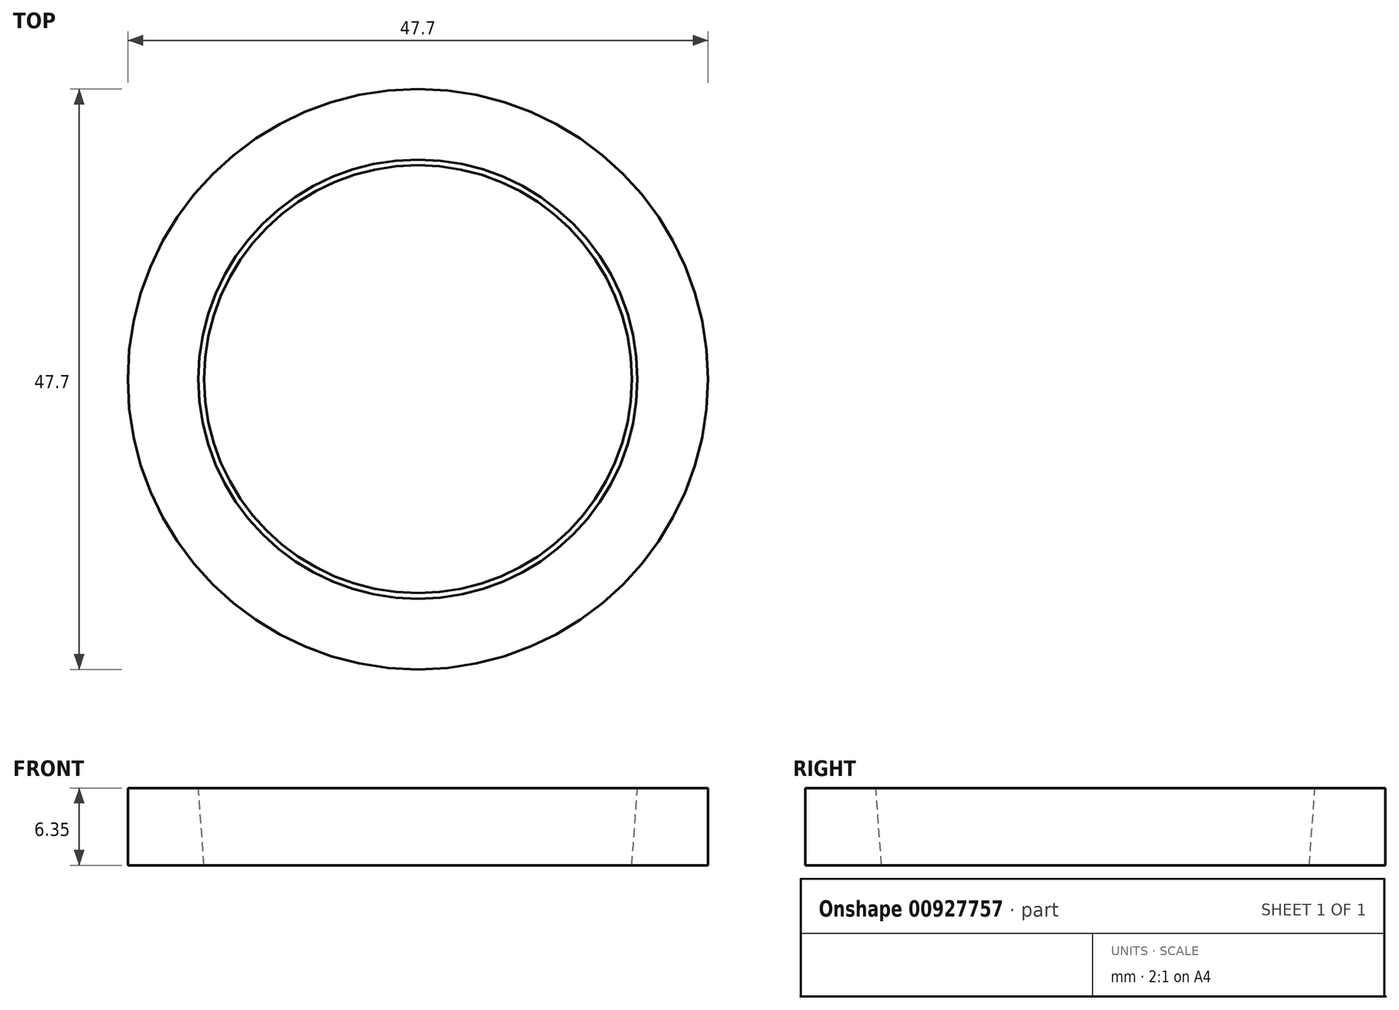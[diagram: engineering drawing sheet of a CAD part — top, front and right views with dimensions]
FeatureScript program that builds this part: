
annotation { "Feature Type Name" : "Feature", "Feature Type Description" : "" }
export const myFeature = defineFeature(function(context is Context, id is Id, definition is map)
    precondition{}
    {
        {
            var Q0;
            Q0=qCreatedBy(makeId("Top.planeOp"),FACE);
            var sketch = newSketch(context, id + "F0", { "sketchPlane" : qUnion([Q0])});
            skCircle(sketch, "E0", {"center": v(0, 0) * mm, "radius": 23.85 * mm});
            skCircle(sketch, "E1", {"center": v(0, 0) * mm, "radius": 15.88 * mm});
            skSolve(sketch);
        }
        {
            var Q0;
            Q0 = qSketchRegion(id + "F0", true);
            extrude(context, id + "F1", {"entities" : qUnion([Q0]), "depth" : 6.35 * mm, "offsetDistance" : 25.4 * mm});
        }
        {
            var Q0;
            Q0=qCreatedBy(makeId("Front.planeOp"),FACE);
            var sketch = newSketch(context, id + "F2", { "sketchPlane" : qUnion([Q0])});
            skLineSegment(sketch, "E2", {"start": v(15.33, 11.5) * mm, "end": v(15.33, -30.82) * mm});
            skLineSegment(sketch, "E3", {"start": v(15.33, -30.82) * mm, "end": v(18.43, 11.5) * mm});
            skLineSegment(sketch, "E4", {"start": v(18.43, 11.5) * mm, "end": v(15.33, 11.5) * mm});
            skSolve(sketch);
        }
        {
            var Q0;
            Q0=qCreatedBy(makeId("Front.planeOp"),FACE);
            var sketch = newSketch(context, id + "F3", { "sketchPlane" : qUnion([Q0])});
            skLineSegment(sketch, "E5", {"start": v(0, 23.55) * mm, "end": v(0, -31.92) * mm, "construction": true});
            skSolve(sketch);
        }
        {
            var Q0;
            Q0=makeQuery(id+"F2.imprint","IMPRINT",FACE,{"disambiguationData":[TD([[makeQuery(id+"F2.imprint","IMPRINT",EDGE,{"derivedFrom":sQuery(id+"F2.wireOp",EDGE,"E2")}),1.0]])]});
            var Q1;
            Q1=sQuery(id+"F3.wireOp",EDGE,"E5");
            revolve(context, id + "F4", {"operationType" : NewBodyOperationType.REMOVE, "surfaceOperationType" : NewSurfaceOperationType.NEW, "entities" : qUnion([Q0]), "axis" : qUnion([Q1]), "revolveType" : RevolveType.FULL, "oppositeDirection" : true});
        }
    });
